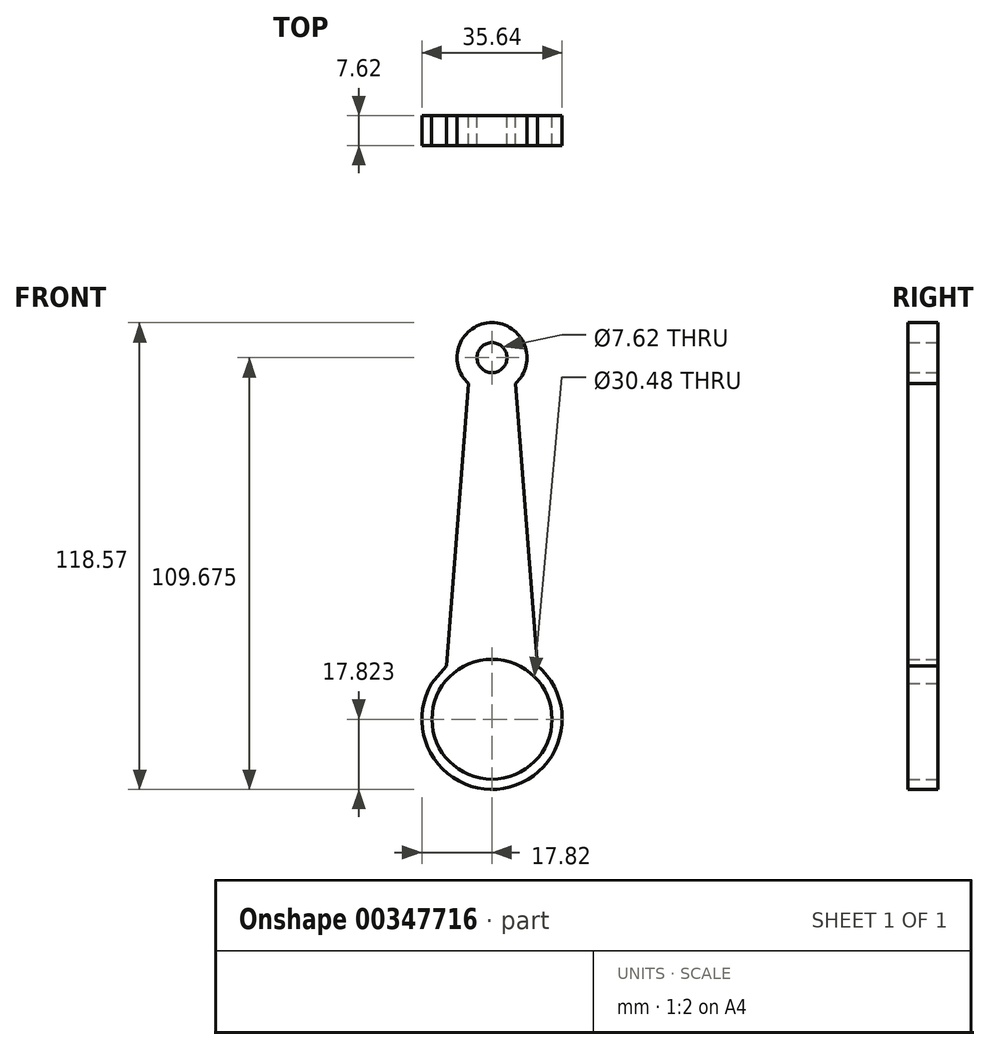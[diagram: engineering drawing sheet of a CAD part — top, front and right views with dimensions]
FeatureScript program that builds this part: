
annotation { "Feature Type Name" : "Feature", "Feature Type Description" : "" }
export const myFeature = defineFeature(function(context is Context, id is Id, definition is map)
    precondition{}
    {
        {
            var Q0;
            Q0=qCreatedBy(makeId("Front.planeOp"),FACE);
            var sketch = newSketch(context, id + "F0", { "sketchPlane" : qUnion([Q0])});
            skCircle(sketch, "E0", {"center": v(0, -46.83) * mm, "radius": 15.24 * mm});
            skCircle(sketch, "E1", {"center": v(0, 45.03) * mm, "radius": 3.81 * mm});
            skCircle(sketch, "E2", {"center": v(0, 45.03) * mm, "radius": 8.9 * mm});
            skCircle(sketch, "E3", {"center": v(0, -46.83) * mm, "radius": 17.82 * mm});
            skLineSegment(sketch, "E4", {"start": v(8.89, 45.03) * mm, "end": v(15.35, -37.77) * mm});
            skLineSegment(sketch, "E5", {"start": v(-15.35, -37.77) * mm, "end": v(-8.92, 45.03) * mm});
            skLineSegment(sketch, "E6", {"start": v(5.98, 38.45) * mm, "end": v(11.58, -33.28) * mm});
            skLineSegment(sketch, "E7", {"start": v(5.98, 38.45) * mm, "end": v(-5.98, 38.45) * mm});
            skLineSegment(sketch, "E8", {"start": v(-5.98, 38.45) * mm, "end": v(-11.58, -33.28) * mm});
            skLineSegment(sketch, "E9", {"start": v(-11.58, -33.28) * mm, "end": v(-15.35, -37.77) * mm});
            skSolve(sketch);
        }
        {
            var Q0;
            Q0=makeQuery(id+"F0.imprint","IMPRINT",FACE,{"disambiguationData":[TD([[makeQuery(id+"F0.imprint","IMPRINT",EDGE,{"derivedFrom":sQuery(id+"F0.wireOp",EDGE,"E1")}),-1.0]])]});
            var Q1;
            {var subQ1=sQuery(id+"F0.wireOp",EDGE,"E6");Q1=makeQuery(id+"F0.imprint","IMPRINT",FACE,{"disambiguationData":[TD([[makeQuery(id+"F0.imprint","IMPRINT",EDGE,{"derivedFrom":subQ1}),-1.0]])]});}
            var Q2;
            {var subQ0=sQuery(id+"F0.wireOp",EDGE,"E7");Q2=makeQuery(id+"F0.imprint","IMPRINT",FACE,{"disambiguationData":[TD([[makeQuery(id+"F0.imprint","IMPRINT",EDGE,{"derivedFrom":subQ0}),1.0]])]});}
            var Q3;
            Q3=makeQuery(id+"F0.imprint","IMPRINT",FACE,{"disambiguationData":[TD([[makeQuery(id+"F0.imprint","IMPRINT",EDGE,{"derivedFrom":sQuery(id+"F0.wireOp",EDGE,"E0")}),-1.0]])]});
            extrude(context, id + "F1", {"entities" : qUnion([Q0, Q1, Q2, Q3]), "endBound" : BoundingType.SYMMETRIC, "depth" : 7.62 * mm});
        }
    });
